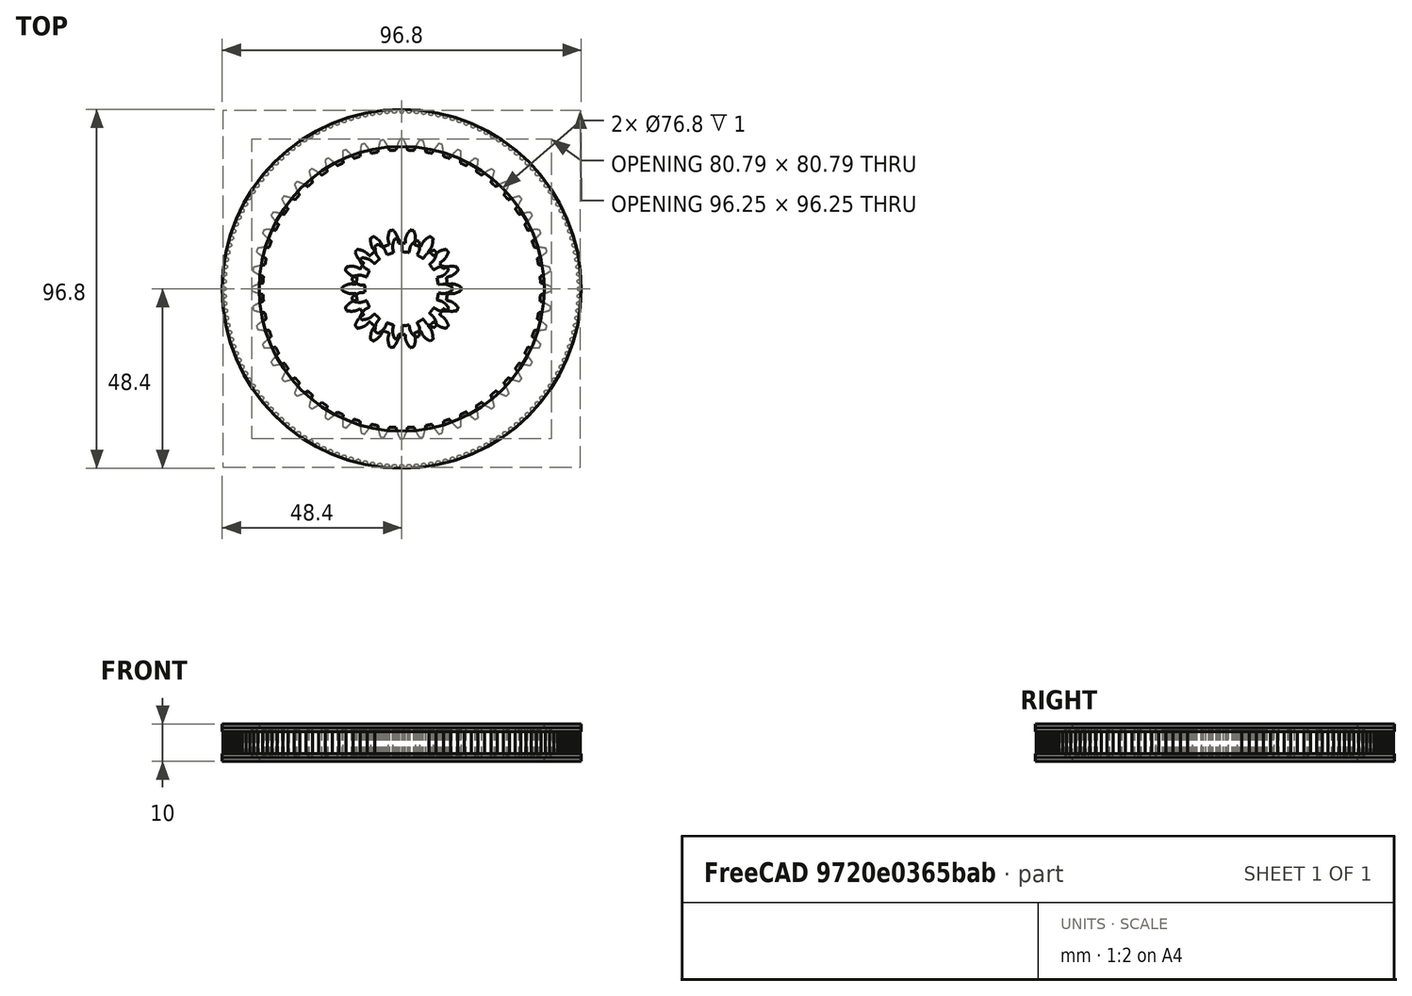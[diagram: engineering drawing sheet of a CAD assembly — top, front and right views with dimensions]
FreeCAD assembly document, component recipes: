
FREECAD ASSEMBLY — COMPONENT RECIPES ("assembly4_planetary_gears")

This assembly document has 4 components, labeled P0..P3 below (a component is one placed body or linked part). 0 of them carry a construction recipe — the FreeCAD feature program that regenerates the part from scratch, quoted from this document or its linked companion documents; the rest are supplied as boundary geometry only. No exploded tour is included for this assembly.
COMPONENT P0 — geometry summary ("Model"; no construction recipe available for this part):
  bounding box: 96.8 x 96.8 x 10.0 mm
  tessellated surface: 9,222 triangles
  volume: 1066666666666666600742544448779472224061444889017356664833983139935149895620844497626853963069164355584 mm^3 (1138632272243576189248097050222704584708125636598584569644772869659412780756371776075496091755216896% of its bounding box)
COMPONENT P1 — geometry summary ("gear_planet"; no construction recipe available for this part):
  bounding box: 27.1 x 27.0 x 8.0 mm
  tessellated surface: 356 triangles
  volume: 106666666666666678723875810244946303232978794407517170250503968894054393579483583256166534276918018048 mm^3 (1821097339944736270955382888834459427256721492300995450989476831518105848742374174743417261880508416% of its bounding box)
  symmetry: 2-fold rotationally symmetric about the x axis; 3-fold rotationally symmetric about the z axis; mirror-symmetric across its y mid-plane, z mid-plane
COMPONENT P2 — geometry summary ("gear_ring"; no construction recipe available for this part):
  bounding box: 96.8 x 96.8 x 10.0 mm
  tessellated surface: 7,726 triangles
  volume: 106666666666666678723875810244946303232978794407517170250503968894054393579483583256166534276918018048 mm^3 (113835568716521612902323187801476844752572024132072819201769064557309436199505106385087265975042048% of its bounding box)
  symmetry: 4-fold rotationally symmetric about the z axis; mirror-symmetric across its x mid-plane, y mid-plane
COMPONENT P3 — geometry summary ("gear_sun"; no construction recipe available for this part):
  bounding box: 32.0 x 31.7 x 8.0 mm
  tessellated surface: 428 triangles
  volume: 106666666666666678723875810244946303232978794407517170250503968894054393579483583256166534276918018048 mm^3 (1316302761417547346769553555631317250318071756839551475748840777381067331888342434226033544356954112% of its bounding box)
  symmetry: 2-fold rotationally symmetric about the x axis; 2-fold rotationally symmetric about the y axis; 6-fold rotationally symmetric about the z axis; mirror-symmetric across its x mid-plane, y mid-plane, z mid-plane
PROVENANCE & LICENSES
A FreeCAD (.FCStd) document from a public repository crawl; recipes are the document's own serialized feature recipes (and, for linked parts, companion documents' recipes).
License: mit.
